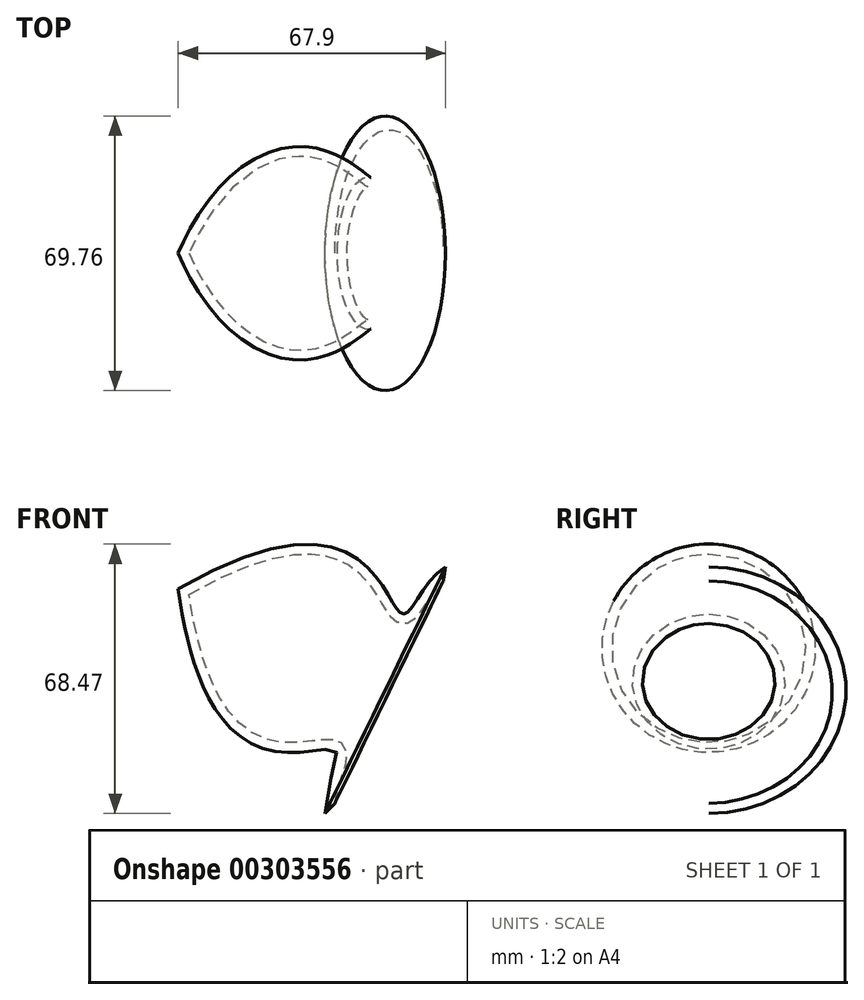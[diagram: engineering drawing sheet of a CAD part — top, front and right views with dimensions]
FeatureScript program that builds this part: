
annotation { "Feature Type Name" : "Feature", "Feature Type Description" : "" }
export const myFeature = defineFeature(function(context is Context, id is Id, definition is map)
    precondition{}
    {
        {
            var Q0;
            Q0=qCreatedBy(makeId("Front.planeOp"),FACE);
            var sketch = newSketch(context, id + "F0", { "sketchPlane" : qUnion([Q0])});
            skLineSegment(sketch, "E0", {"start": v(44.7, 0) * mm, "end": v(-25.08, 34.07) * mm});
            skFitSpline(sketch, "E1", {"points": [v(-25.08, 34.07) * mm, v(32.79, 27.96) * mm, v(54, 37.28) * mm], "startDerivative": vector(252.95, 147.48) * mm, "endDerivative": vector(94.22, -87.13) * mm});
            skFitSpline(sketch, "E2", {"points": [v(54, 37.28) * mm, v(60.3, 17.9) * mm, v(44.7, 0) * mm], "startDerivative": vector(23.21, -42.76) * mm, "endDerivative": vector(-41.36, -33) * mm});
            skSolve(sketch);
        }
        {
            var Q0;
            Q0=makeQuery(id+"F0.imprint","IMPRINT",FACE,{"disambiguationData":[TD([[makeQuery(id+"F0.imprint","IMPRINT",EDGE,{"derivedFrom":sQuery(id+"F0.wireOp",EDGE,"E0")}),-1.0]])]});
            var Q1;
            Q1=sQuery(id+"F0.wireOp",EDGE,"E0");
            revolve(context, id + "F1", {"entities" : qUnion([Q0]), "axis" : qUnion([Q1]), "revolveType" : RevolveType.FULL});
        }
        {
            var Q0;
            Q0=makeQuery(id+"F1.opRevolve","SWEPT_FACE",FACE,{"disambiguationData":[OSD([sQuery(id+"F0.wireOp",EDGE,"E2")])]});
            shell(context, id + "F2", {"entities" : qUnion([Q0]), "thickness" : 2.5 * mm});
        }
        {
            var Q0;
            Q0=makeQuery(id+"F2.opShell","OFFSET_EDGE",EDGE,{"disambiguationData":[OSD([sQuery(id+"F0.wireOp",EDGE,"E1"),sQuery(id+"F0.wireOp",EDGE,"E2")])]});
            chamfer(context, id + "F3", {"entities" : qUnion([Q0]), "width" : 15 * mm, "tangentPropagation" : true});
        }
    });
